# Revit family: Скамейка стальная вокруг дерева или столба «Экспресс».Арт 10728
name_source: partatom
category: Антураж
revit_build: Autodesk Revit 2018 (Build: 20180423_1000(x64)
units: mm (PartAtom-declared; Revit-internal decimal feet)

## family parameters
Всегда вертикально = Да
Источник визуального образа = Геометрия семейства
На основе рабочей плоскости = Нет
Общий = Нет
При загрузке вырезать с полостями = Нет
Точка расчета площади = Нет

## types (2) — shared parameters
URL = https://hobbyka.ru
Артикул товара = Арт. 10728
Высота = 1030 мм
Группа модели = Скамейки
Диаметр = 1300 мм
Длина = 1300 мм
Изготовитель = ООО «Хоббика»
Материал изделия = Сталь, дерево
Цвет каркаса = Сталь
Цвет лавки = Дерево
Ширина = 1300 мм

## per-type parameters (varying)
| type | Без кашпо | Изображение типоразмера | С кашпо |
| Скамейка стальная вокруг дерева или столба «Экспресс». Версия без кашпо | Да | Скамейка стальная вокруг дерева или столба «Экспресс» Арт 10728 без кашпо.jpg | Нет |
| Скамейка стальная вокруг дерева или столба «Экспресс». Версия с кашпо | Нет | Скамейка стальная вокруг дерева или столба «Экспресс» Арт 10728 с кашпо.jpg | Да |

note: column(s) folded — value = type name in every type: Описание
